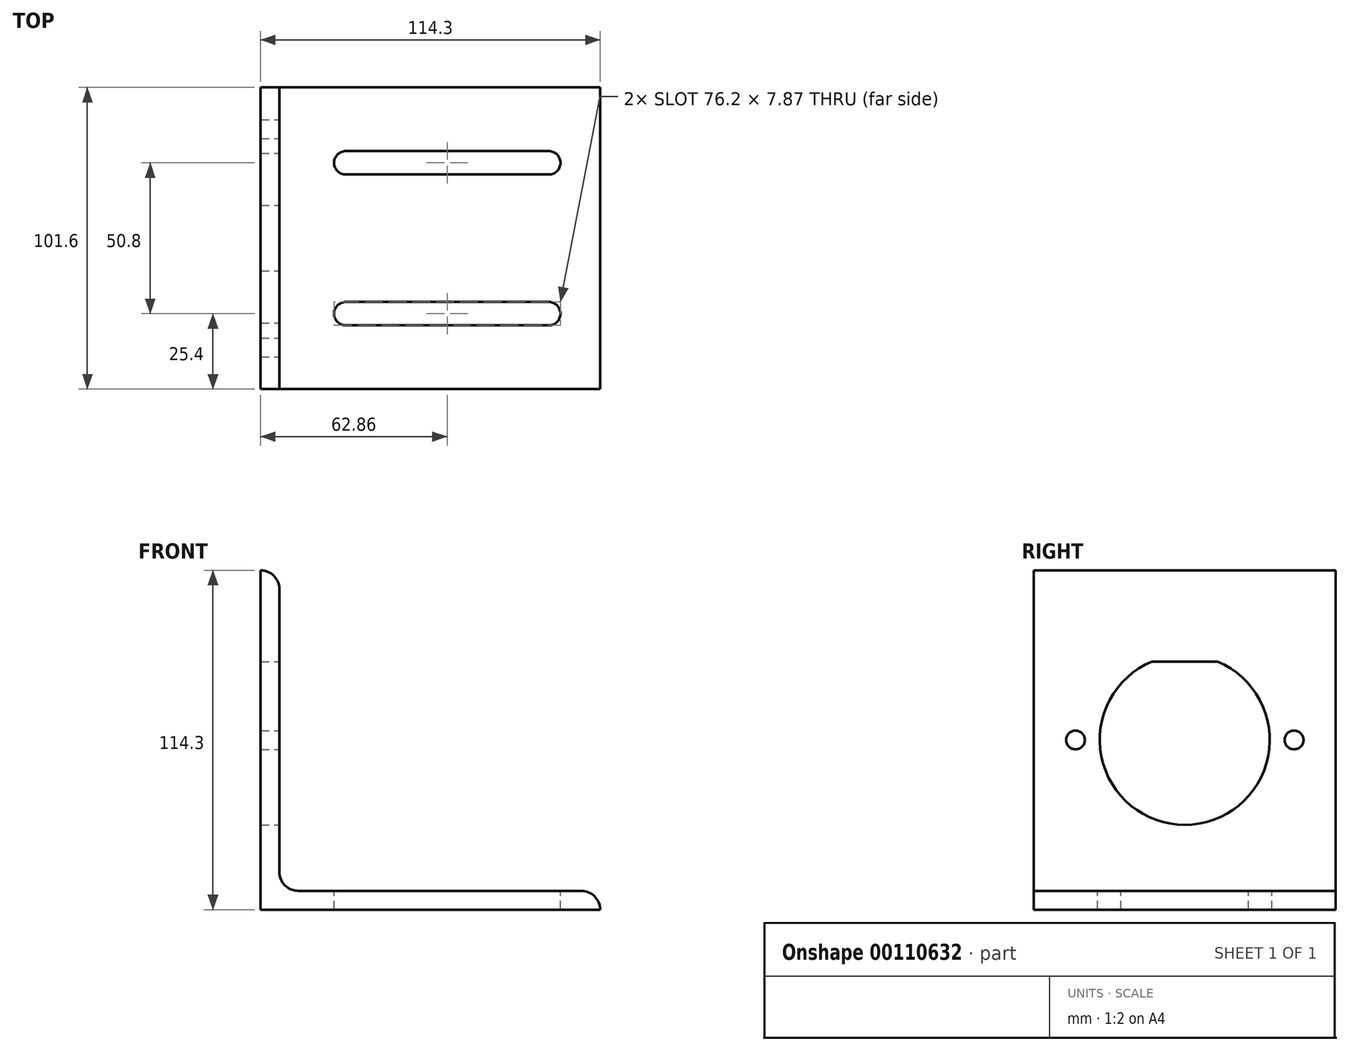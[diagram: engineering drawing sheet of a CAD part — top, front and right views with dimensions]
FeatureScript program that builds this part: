
annotation { "Feature Type Name" : "Feature", "Feature Type Description" : "" }
export const myFeature = defineFeature(function(context is Context, id is Id, definition is map)
    precondition{}
    {
        {
            var Q0;
            Q0=qCreatedBy(makeId("Front.planeOp"),FACE);
            var sketch = newSketch(context, id + "F0", { "sketchPlane" : qUnion([Q0])});
            skLineSegment(sketch, "E0", {"start": v(-85.87, 52.44) * mm, "end": v(-85.87, -61.86) * mm});
            skLineSegment(sketch, "E1", {"start": v(-85.87, -61.86) * mm, "end": v(28.43, -61.86) * mm});
            skLineSegment(sketch, "E2", {"start": v(28.43, -61.86) * mm, "end": v(28.43, -55.5) * mm});
            skLineSegment(sketch, "E3", {"start": v(28.43, -55.5) * mm, "end": v(-79.52, -55.5) * mm});
            skLineSegment(sketch, "E4", {"start": v(-79.52, -55.5) * mm, "end": v(-79.52, 52.44) * mm});
            skLineSegment(sketch, "E5", {"start": v(-79.52, 52.44) * mm, "end": v(-85.87, 52.44) * mm});
            skSolve(sketch);
        }
        {
            var Q0;
            Q0 = qSketchRegion(id + "F0", true);
            extrude(context, id + "F1", {"entities" : qUnion([Q0]), "depth" : 101.6 * mm});
        }
        {
            var Q0;
            Q0=makeQuery(id+"F1.opExtrude","SWEPT_EDGE",EDGE,{"disambiguationData":[OSD([sQuery(id+"F0.wireOp",EDGE,"E4"),sQuery(id+"F0.wireOp",EDGE,"E5")])]});
            var Q1;
            Q1=makeQuery(id+"F1.opExtrude","SWEPT_EDGE",EDGE,{"disambiguationData":[OSD([sQuery(id+"F0.wireOp",EDGE,"E2"),sQuery(id+"F0.wireOp",EDGE,"E3")])]});
            var Q2;
            Q2=makeQuery(id+"F1.opExtrude","SWEPT_EDGE",EDGE,{"disambiguationData":[OSD([sQuery(id+"F0.wireOp",EDGE,"E3"),sQuery(id+"F0.wireOp",EDGE,"E4")])]});
            fillet(context, id + "F2", {"entities" : qUnion([Q0, Q1, Q2]), "radius" : 6.35 * mm, "tangentPropagation" : true, "allowEdgeOverflow" : false});
        }
        {
            var Q0;
            Q0=makeQuery(id+"F1.opExtrude","SWEPT_FACE",FACE,{"disambiguationData":[OSD([sQuery(id+"F0.wireOp",EDGE,"E4")])]});
            var sketch = newSketch(context, id + "F3", { "sketchPlane" : qUnion([Q0])});
            skArc(sketch, "E6", {"start": v(-61.82, 21.68) * mm, "mid": v(-50.8, -33.3) * mm, "end": v(-39.78, 21.68) * mm});
            skCircle(sketch, "E7", {"center": v(-87.58, -4.7) * mm, "radius": 3.18 * mm});
            skCircle(sketch, "E8", {"center": v(-14.02, -4.7) * mm, "radius": 3.18 * mm});
            skLineSegment(sketch, "E9", {"start": v(-61.82, 21.68) * mm, "end": v(-39.78, 21.68) * mm});
            skSolve(sketch);
        }
        {
            var Q0;
            Q0 = qSketchRegion(id + "F3", true);
            extrude(context, id + "F4", {"entities" : qUnion([Q0]), "operationType" : NewBodyOperationType.REMOVE, "oppositeDirection" : true, "depth" : 25.4 * mm});
        }
        {
            var Q0;
            Q0=makeQuery(id+"F1.opExtrude","SWEPT_FACE",FACE,{"disambiguationData":[OSD([sQuery(id+"F0.wireOp",EDGE,"E3")])]});
            var sketch = newSketch(context, id + "F5", { "sketchPlane" : qUnion([Q0])});
            skLineSegment(sketch, "E10", {"start": v(-57.17, -80.14) * mm, "end": v(11.15, -80.14) * mm});
            skLineSegment(sketch, "E11", {"start": v(-57.17, -72.26) * mm, "end": v(11.15, -72.26) * mm});
            skLineSegment(sketch, "E12", {"start": v(-57.17, -29.34) * mm, "end": v(11.15, -29.34) * mm});
            skLineSegment(sketch, "E13", {"start": v(-57.17, -21.46) * mm, "end": v(11.15, -21.46) * mm});
            skArc(sketch, "E14", {"start": v(-57.17, -72.26) * mm, "mid": v(-61.1, -76.2) * mm, "end": v(-57.17, -80.14) * mm});
            skArc(sketch, "E15", {"start": v(11.15, -80.14) * mm, "mid": v(15.1, -76.2) * mm, "end": v(11.15, -72.26) * mm});
            skArc(sketch, "E16", {"start": v(-57.17, -21.46) * mm, "mid": v(-61.1, -25.4) * mm, "end": v(-57.17, -29.34) * mm});
            skArc(sketch, "E17", {"start": v(11.15, -29.34) * mm, "mid": v(15.1, -25.4) * mm, "end": v(11.15, -21.46) * mm});
            skSolve(sketch);
        }
        {
            var Q0;
            Q0 = qSketchRegion(id + "F5", true);
            extrude(context, id + "F6", {"entities" : qUnion([Q0]), "operationType" : NewBodyOperationType.REMOVE, "oppositeDirection" : true, "depth" : 25.4 * mm});
        }
    });
